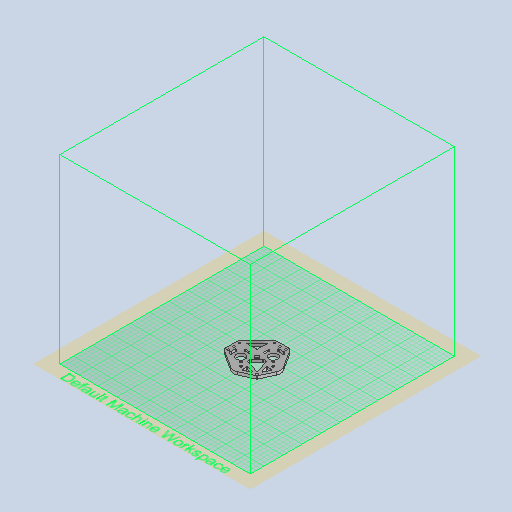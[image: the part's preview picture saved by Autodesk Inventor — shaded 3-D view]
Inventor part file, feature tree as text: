
AUTODESK INVENTOR PART (.ipt)
format: ipt  version: 2022 (Build 260153000, 153)  size: 777,728 bytes
history: native  units: in
note: dims shown in document units (in); Inventor stores cm internally (conversion verified against a paired STEP export)
features: extrude x5, sketch x5, other x4, projected_geometry x3, chamfer x2, reference x2, fillet x1
ambient origin geometry x8: Origin, YZ Plane, XZ Plane, XY Plane, X Axis, Y Axis, Z Axis, Center Point
bodies: Solid1 (feature_tree)
feature tree (22):
  extrude  "Extrusion1"  Depth=0.25in TaperAngle=0.0deg
  extrude  "Extrusion2"  Depth=0.05in
  extrude  "Extrusion3"  Depth=0.5in
  fillet  "Fillet1"  Radius=0.5in
  extrude  "Extrusion4"  Depth=0.25in
  extrude  "Extrusion5"  Depth=0.5in
  chamfer  "Chamfer1"  Distance=0.5in
  chamfer  "Chamfer2"  Angle=45.0deg  [1 undecoded]
  sketch  "Sketch1"  dims[d9=0.75in d11=0.25in d12=0.0in]
  reference  "Reference1"
  sketch  "Sketch2"  dims[d14=0.05in d15=0.0in d16=0.1679in]
  projected_geometry  "Projected Loop1"
  projected_geometry  "Projected Loop2"
  sketch  "Sketch3"  dims[d17=1.1811in d19=0.5in d20=0.3937in d22=1.0in d26=0.1938in d28=0.5in]
  projected_geometry  "Projected Loop3"
  sketch  "Sketch4"  dims[d29=0.25in d30=0.25in]
  reference  "Reference2"
  sketch  "Sketch5"  dims[d31=0.25in d33=0.5in d34=0.5in d35=45.0deg d36=0.25in d37=45.0deg d38=0.25in d39=0.5in d40=0.5in d41=0.25in d42=0.25in d43=0.5in d44=0.5in d45=0.0in d46=0.0in d47=0.0394in d48=0.261in d49=1.0in d50=0.0in d51=0.3957in d52=0.0787in d53=0.0in d54=0.0236in d55=0.125in d56=45.0deg d57=0.1679in d58=0.0236in d59=0.125in d60=45.0deg d61=0.1679in d62=0.1679in]
  other  "<userpath>\Documents\CAD\guardSwerve1\Assembly1.iam"
  other  "Assembly1.iam"
  other  "uppermidblock:1"
  other  "Undercarriage:1"
note: 1 required parameter value undecoded (feature->parameter linkage not recoverable at this tier; creation-order binding heuristic only, values carry confidence <= 0.55)
